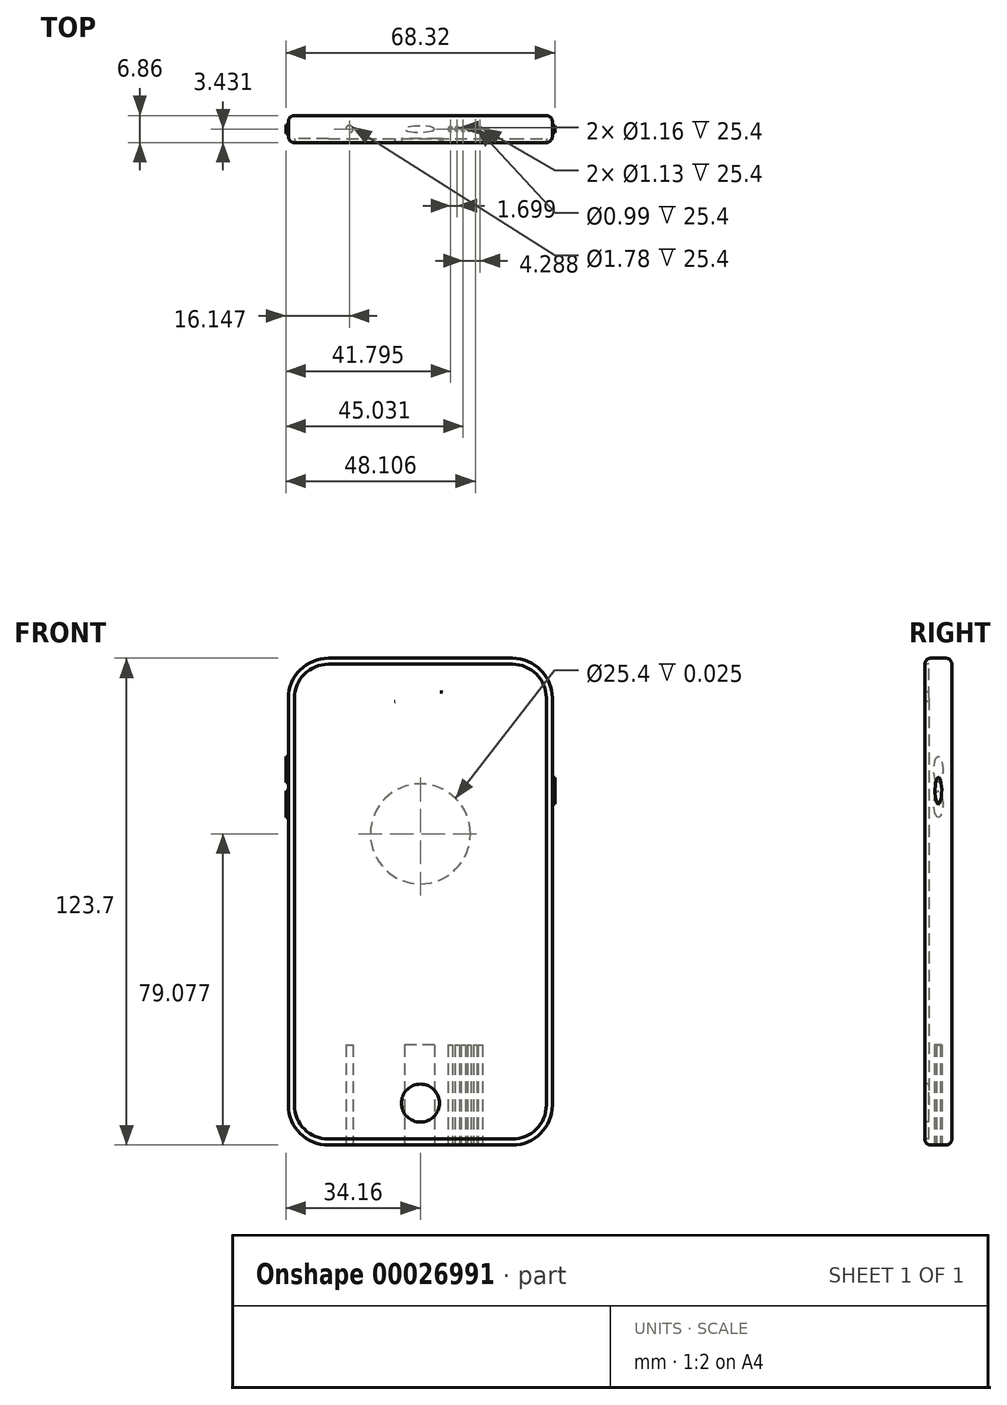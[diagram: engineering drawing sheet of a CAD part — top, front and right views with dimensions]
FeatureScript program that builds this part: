
annotation { "Feature Type Name" : "Feature", "Feature Type Description" : "" }
export const myFeature = defineFeature(function(context is Context, id is Id, definition is map)
    precondition{}
    {
        {
            var Q0;
            Q0=qCreatedBy(makeId("Front.planeOp"),FACE);
            var sketch = newSketch(context, id + "F0", { "sketchPlane" : qUnion([Q0])});
            skLineSegment(sketch, "E0.bottom", {"start": v(-33.33, 66.72) * mm, "end": v(33.73, 66.72) * mm});
            skLineSegment(sketch, "E0.top", {"start": v(-33.33, -56.98) * mm, "end": v(33.73, -56.98) * mm});
            skLineSegment(sketch, "E0.left", {"start": v(-33.33, 66.72) * mm, "end": v(-33.33, -56.98) * mm});
            skLineSegment(sketch, "E0.right", {"start": v(33.73, 66.72) * mm, "end": v(33.73, -56.98) * mm});
            skSolve(sketch);
        }
        {
            var Q0;
            Q0 = qSketchRegion(id + "F0", true);
            extrude(context, id + "F1", {"entities" : qUnion([Q0]), "depth" : 6.86 * mm});
        }
        {
            var Q0;
            Q0=makeQuery(id+"F1.opExtrude","SWEPT_EDGE",EDGE,{"disambiguationData":[OSD([sQuery(id+"F0.wireOp",EDGE,"E0.bottom"),sQuery(id+"F0.wireOp",EDGE,"E0.left")])]});
            var Q1;
            Q1=makeQuery(id+"F1.opExtrude","SWEPT_EDGE",EDGE,{"disambiguationData":[OSD([sQuery(id+"F0.wireOp",EDGE,"E0.bottom"),sQuery(id+"F0.wireOp",EDGE,"E0.right")])]});
            fillet(context, id + "F2", {"entities" : qUnion([Q0, Q1]), "radius" : 10.16 * mm, "tangentPropagation" : true, "allowEdgeOverflow" : false});
        }
        {
            var Q0;
            Q0=makeQuery(id+"F1.opExtrude","SWEPT_EDGE",EDGE,{"disambiguationData":[OSD([sQuery(id+"F0.wireOp",EDGE,"E0.top"),sQuery(id+"F0.wireOp",EDGE,"E0.left")])]});
            var Q1;
            Q1=makeQuery(id+"F1.opExtrude","SWEPT_EDGE",EDGE,{"disambiguationData":[OSD([sQuery(id+"F0.wireOp",EDGE,"E0.top"),sQuery(id+"F0.wireOp",EDGE,"E0.right")])]});
            fillet(context, id + "F3", {"entities" : qUnion([Q0, Q1]), "radius" : 10.16 * mm, "tangentPropagation" : true, "allowEdgeOverflow" : false});
        }
        {
            var Q0;
            Q0=makeQuery(id+"F1.opExtrude","CAP_EDGE",EDGE,{"disambiguationData":[OSD([sQuery(id+"F0.wireOp",EDGE,"E0.right")])],"isStart":true});
            fillet(context, id + "F4", {"entities" : qUnion([Q0]), "radius" : 1.52 * mm, "tangentPropagation" : true, "allowEdgeOverflow" : false});
        }
        {
            var Q0;
            Q0=makeQuery(id+"F1.opExtrude","CAP_EDGE",EDGE,{"disambiguationData":[OSD([sQuery(id+"F0.wireOp",EDGE,"E0.right")])],"isStart":false});
            fillet(context, id + "F5", {"entities" : qUnion([Q0]), "radius" : 1.52 * mm, "tangentPropagation" : true, "allowEdgeOverflow" : false});
        }
        {
            var Q0;
            Q0=makeQuery(id+"F1.opExtrude","CAP_FACE",FACE,{"disambiguationData":[OSD([sQuery(id+"F0.wireOp",EDGE,"E0.bottom"),sQuery(id+"F0.wireOp",EDGE,"E0.top"),sQuery(id+"F0.wireOp",EDGE,"E0.left"),sQuery(id+"F0.wireOp",EDGE,"E0.right")])],"isStart":false});
            var sketch = newSketch(context, id + "F6", { "sketchPlane" : qUnion([Q0])});
            skLineSegment(sketch, "E1.0", {"start": v(30.68, 48.43) * mm, "end": v(-30.28, 48.43) * mm});
            skLineSegment(sketch, "E2.0", {"start": v(-30.28, -38.7) * mm, "end": v(30.68, -38.7) * mm});
            skLineSegment(sketch, "E3.0", {"start": v(-30.28, 48.43) * mm, "end": v(-30.28, -38.7) * mm});
            skLineSegment(sketch, "E4.0", {"start": v(30.68, -38.7) * mm, "end": v(30.68, 48.43) * mm});
            skCircle(sketch, "E5", {"center": v(0.2, -46.31) * mm, "radius": 5.46 * mm});
            skLineSegment(sketch, "E6.0", {"start": v(23.57, 56.81) * mm, "end": v(6.78, 56.81) * mm});
            skCircle(sketch, "E7", {"center": v(-15.3, 56.81) * mm, "radius": 2.54 * mm});
            skCircle(sketch, "E8", {"center": v(0, 61.1) * mm, "radius": 1.12 * mm});
            skLineSegment(sketch, "E9", {"start": v(-6.37, 55.68) * mm, "end": v(5.57, 55.68) * mm});
            skLineSegment(sketch, "E10", {"start": v(5.86, 58.11) * mm, "end": v(-6.43, 58.11) * mm});
            skArc(sketch, "E11", {"start": v(-6.14, 58.11) * mm, "mid": v(-7.5, 56.93) * mm, "end": v(-6.2, 55.68) * mm});
            skArc(sketch, "E12", {"start": v(5.53, 55.68) * mm, "mid": v(6.77, 57.07) * mm, "end": v(5.23, 58.11) * mm});
            skPoint(sketch, "E13.orphan", {"position": v(-10.28, 58.11) * mm});
            skPoint(sketch, "E14.end.orphan", {"position": v(9.44, 58.11) * mm});
            skLineSegment(sketch, "E15.trimOffspring", {"start": v(-7.5, 56.81) * mm, "end": v(-23.17, 56.81) * mm});
            skCircle(sketch, "E16", {"center": v(0.2, -46.31) * mm, "radius": 4.82 * mm});
            skSolve(sketch);
        }
        {
            var Q0;
            Q0=makeQuery(id+"F6.imprint","IMPRINT",FACE,{"disambiguationData":[TD([[makeQuery(id+"F6.imprint","IMPRINT",EDGE,{"derivedFrom":sQuery(id+"F6.wireOp",EDGE,"E8")}),1.0]])]});
            var Q1;
            Q1=makeQuery(id+"F6.imprint","IMPRINT",FACE,{"disambiguationData":[TD([[makeQuery(id+"F6.imprint","IMPRINT",EDGE,{"derivedFrom":sQuery(id+"F6.wireOp",EDGE,"E5")}),1.0]])]});
            var Q2;
            {var subQ0=sQuery(id+"F6.wireOp",EDGE,"E15.trimOffspring");var subQ1=sQuery(id+"F6.wireOp",EDGE,"E7");var subQ3=makeQuery(id+"F6.imprint","INTERSECT",VERTEX,{"disambiguationData":[OD(0.0)],"derivedFrom":[subQ1,subQ0]});Q2=makeQuery(id+"F6.imprint","IMPRINT",FACE,{"disambiguationData":[TD([[makeQuery(id+"F6.imprint","IMPRINT",EDGE,{"disambiguationData":[TD([[subQ3,1.0]])],"derivedFrom":subQ1}),1.0]])]});}
            var Q3;
            {var subQ0=sQuery(id+"F6.wireOp",EDGE,"E15.trimOffspring");var subQ1=sQuery(id+"F6.wireOp",EDGE,"E7");var subQ3=makeQuery(id+"F6.imprint","INTERSECT",VERTEX,{"disambiguationData":[OD(0.0)],"derivedFrom":[subQ1,subQ0]});Q3=makeQuery(id+"F6.imprint","IMPRINT",FACE,{"disambiguationData":[TD([[makeQuery(id+"F6.imprint","IMPRINT",EDGE,{"disambiguationData":[TD([[subQ3,-1.0]])],"derivedFrom":subQ1}),1.0]])]});}
            var Q4;
            {var subQ0=sQuery(id+"F6.wireOp",EDGE,"E11");var subQ1=sQuery(id+"F6.wireOp",EDGE,"E9");var subQ3=makeQuery(id+"F6.imprint","INTERSECT",VERTEX,{"disambiguationData":[OD(0.0)],"derivedFrom":[subQ1,subQ0]});Q4=makeQuery(id+"F6.imprint","IMPRINT",FACE,{"disambiguationData":[TD([[makeQuery(id+"F6.imprint","IMPRINT",EDGE,{"disambiguationData":[TD([[subQ3,-1.0]])],"derivedFrom":subQ1}),-1.0]])]});}
            var Q5;
            {var subQ0=sQuery(id+"F6.wireOp",EDGE,"E12");var subQ1=sQuery(id+"F6.wireOp",EDGE,"E9");var subQ3=makeQuery(id+"F6.imprint","INTERSECT",VERTEX,{"disambiguationData":[OD(0.0)],"derivedFrom":[subQ1,subQ0]});Q5=makeQuery(id+"F6.imprint","IMPRINT",FACE,{"disambiguationData":[TD([[makeQuery(id+"F6.imprint","IMPRINT",EDGE,{"disambiguationData":[TD([[subQ3,1.0]])],"derivedFrom":subQ1}),-1.0]])]});}
            var Q6;
            {var subQ0=sQuery(id+"F6.wireOp",EDGE,"E12");var subQ1=sQuery(id+"F6.wireOp",EDGE,"E10");var subQ3=makeQuery(id+"F6.imprint","INTERSECT",VERTEX,{"disambiguationData":[OD(0.0)],"derivedFrom":[subQ1,subQ0]});Q6=makeQuery(id+"F6.imprint","IMPRINT",FACE,{"disambiguationData":[TD([[makeQuery(id+"F6.imprint","IMPRINT",EDGE,{"disambiguationData":[TD([[subQ3,-1.0]])],"derivedFrom":subQ1}),-1.0]])]});}
            var Q7;
            {var subQ0=sQuery(id+"F6.wireOp",EDGE,"E11");var subQ1=sQuery(id+"F6.wireOp",EDGE,"E10");var subQ3=makeQuery(id+"F6.imprint","INTERSECT",VERTEX,{"disambiguationData":[OD(0.0)],"derivedFrom":[subQ1,subQ0]});Q7=makeQuery(id+"F6.imprint","IMPRINT",FACE,{"disambiguationData":[TD([[makeQuery(id+"F6.imprint","IMPRINT",EDGE,{"disambiguationData":[TD([[subQ3,1.0]])],"derivedFrom":subQ1}),-1.0]])]});}
            var Q8;
            {var subQ0=sQuery(id+"F6.wireOp",EDGE,"E11");var subQ1=makeQuery(id+"F6.imprint","IMPRINT",VERTEX,{"derivedFrom":subQ0});Q8=makeQuery(id+"F6.imprint","IMPRINT",FACE,{"disambiguationData":[TD([[makeQuery(id+"F6.imprint","IMPRINT",EDGE,{"disambiguationData":[TD([[subQ1,1.0]])],"derivedFrom":subQ0}),1.0]])]});}
            var Q9;
            Q9=makeQuery(id+"F6.imprint","IMPRINT",FACE,{"disambiguationData":[TD([[makeQuery(id+"F6.imprint","IMPRINT",EDGE,{"derivedFrom":sQuery(id+"F6.wireOp",EDGE,"E1.0")}),1.0]])]});
            extrude(context, id + "F7", {"entities" : qUnion([Q0, Q1, Q2, Q3, Q4, Q5, Q6, Q7, Q8, Q9]), "operationType" : NewBodyOperationType.REMOVE, "oppositeDirection" : true, "depth" : 1.02 * mm});
        }
        {
            var Q0;
            Q0=makeQuery(id+"F1.opExtrude","SWEPT_FACE",FACE,{"disambiguationData":[OSD([sQuery(id+"F0.wireOp",EDGE,"E0.top")])]});
            var sketch = newSketch(context, id + "F8", { "sketchPlane" : qUnion([Q0])});
            skLineSegment(sketch, "E17", {"start": v(-23.17, 5.33) * mm, "end": v(-23.17, 1.52) * mm});
            skCircle(sketch, "E18", {"center": v(-17.81, 3.43) * mm, "radius": 0.9 * mm});
            skLineSegment(sketch, "E19", {"start": v(-23.17, 5.33) * mm, "end": v(23.57, 5.33) * mm});
            skEllipse(sketch, "E20", {"center": v(0, 3.43) * mm, "majorRadius": 3.79 * mm, "minorRadius": 0.94 * mm, "majorAxis": v(1, 0)});
            skCircle(sketch, "E21", {"center": v(7.83, 3.43) * mm, "radius": 0.58 * mm});
            skCircle(sketch, "E22", {"center": v(9.53, 3.43) * mm, "radius": 0.58 * mm});
            skCircle(sketch, "E23", {"center": v(11.07, 3.43) * mm, "radius": 0.56 * mm});
            skCircle(sketch, "E24", {"center": v(12.6, 3.43) * mm, "radius": 0.49 * mm});
            skCircle(sketch, "E25", {"center": v(14.15, 3.43) * mm, "radius": 0.5 * mm});
            skCircle(sketch, "E26", {"center": v(15.36, 3.43) * mm, "radius": 0.56 * mm});
            skSolve(sketch);
        }
        {
            var Q0;
            Q0=makeQuery(id+"F8.imprint","IMPRINT",FACE,{"disambiguationData":[TD([[makeQuery(id+"F8.imprint","IMPRINT",EDGE,{"derivedFrom":sQuery(id+"F8.wireOp",EDGE,"E18")}),1.0]])]});
            var Q1;
            Q1=makeQuery(id+"F8.imprint","IMPRINT",FACE,{"disambiguationData":[TD([[makeQuery(id+"F8.imprint","IMPRINT",EDGE,{"derivedFrom":sQuery(id+"F8.wireOp",EDGE,"E20")}),1.0]])]});
            var Q2;
            Q2=makeQuery(id+"F8.imprint","IMPRINT",FACE,{"disambiguationData":[TD([[makeQuery(id+"F8.imprint","IMPRINT",EDGE,{"derivedFrom":sQuery(id+"F8.wireOp",EDGE,"E22")}),1.0]])]});
            var Q3;
            Q3=makeQuery(id+"F8.imprint","IMPRINT",FACE,{"disambiguationData":[TD([[makeQuery(id+"F8.imprint","IMPRINT",EDGE,{"derivedFrom":sQuery(id+"F8.wireOp",EDGE,"E23")}),1.0]])]});
            var Q4;
            Q4=makeQuery(id+"F8.imprint","IMPRINT",FACE,{"disambiguationData":[TD([[makeQuery(id+"F8.imprint","IMPRINT",EDGE,{"derivedFrom":sQuery(id+"F8.wireOp",EDGE,"E24")}),1.0]])]});
            var Q5;
            Q5=makeQuery(id+"F8.imprint","IMPRINT",FACE,{"disambiguationData":[TD([[makeQuery(id+"F8.imprint","IMPRINT",EDGE,{"derivedFrom":sQuery(id+"F8.wireOp",EDGE,"E25")}),1.0]])]});
            var Q6;
            Q6=makeQuery(id+"F8.imprint","IMPRINT",FACE,{"disambiguationData":[TD([[makeQuery(id+"F8.imprint","IMPRINT",EDGE,{"derivedFrom":sQuery(id+"F8.wireOp",EDGE,"E26")}),1.0]])]});
            var Q7;
            Q7=makeQuery(id+"F8.imprint","IMPRINT",FACE,{"disambiguationData":[TD([[makeQuery(id+"F8.imprint","IMPRINT",EDGE,{"derivedFrom":sQuery(id+"F8.wireOp",EDGE,"E21")}),1.0]])]});
            extrude(context, id + "F9", {"entities" : qUnion([Q0, Q1, Q2, Q3, Q4, Q5, Q6, Q7]), "operationType" : NewBodyOperationType.REMOVE, "oppositeDirection" : true, "depth" : 25.4 * mm});
        }
        {
            var Q0;
            Q0=makeQuery(id+"F1.opExtrude","SWEPT_FACE",FACE,{"disambiguationData":[OSD([sQuery(id+"F0.wireOp",EDGE,"E0.right")])]});
            var sketch = newSketch(context, id + "F10", { "sketchPlane" : qUnion([Q0])});
            skEllipse(sketch, "E27", {"center": v(-3.43, 33.07) * mm, "majorRadius": 3.36 * mm, "minorRadius": 0.85 * mm, "majorAxis": v(0, -1)});
            skSolve(sketch);
        }
        {
            var Q0;
            Q0=makeQuery(id+"F10.imprint","IMPRINT",FACE,{"disambiguationData":[TD([[makeQuery(id+"F10.imprint","IMPRINT",EDGE,{"derivedFrom":sQuery(id+"F10.wireOp",EDGE,"E27")}),1.0]])]});
            extrude(context, id + "F11", {"entities" : qUnion([Q0]), "operationType" : NewBodyOperationType.ADD, "depth" : 0.64 * mm});
        }
        {
            var Q0;
            Q0=makeQuery(id+"F1.opExtrude","SWEPT_FACE",FACE,{"disambiguationData":[OSD([sQuery(id+"F0.wireOp",EDGE,"E0.left")])]});
            var sketch = newSketch(context, id + "F12", { "sketchPlane" : qUnion([Q0])});
            skEllipse(sketch, "E28", {"center": v(3.43, 38.42) * mm, "majorRadius": 3.32 * mm, "minorRadius": 1.12 * mm, "majorAxis": v(0, -1)});
            skEllipse(sketch, "E29", {"center": v(3.43, 29.66) * mm, "majorRadius": 3.35 * mm, "minorRadius": 1.12 * mm, "majorAxis": v(0, -1)});
            skSolve(sketch);
        }
        {
            var Q0;
            Q0 = qSketchRegion(id + "F12", true);
            extrude(context, id + "F13", {"entities" : qUnion([Q0]), "operationType" : NewBodyOperationType.ADD, "depth" : 0.64 * mm});
        }
        {
            var Q0;
            Q0=makeQuery(id+"F1.opExtrude","CAP_FACE",FACE,{"disambiguationData":[OSD([sQuery(id+"F0.wireOp",EDGE,"E0.bottom"),sQuery(id+"F0.wireOp",EDGE,"E0.top"),sQuery(id+"F0.wireOp",EDGE,"E0.left"),sQuery(id+"F0.wireOp",EDGE,"E0.right")])],"isStart":true});
            var sketch = newSketch(context, id + "F14", { "sketchPlane" : qUnion([Q0])});
            skCircle(sketch, "E30", {"center": v(-0.2, 22.1) * mm, "radius": 12.7 * mm});
            skSolve(sketch);
        }
        {
            var Q0;
            Q0=makeQuery(id+"F14.imprint","IMPRINT",FACE,{"disambiguationData":[TD([[makeQuery(id+"F14.imprint","IMPRINT",EDGE,{"derivedFrom":sQuery(id+"F14.wireOp",EDGE,"E30")}),1.0]])]});
            extrude(context, id + "F15", {"entities" : qUnion([Q0]), "operationType" : NewBodyOperationType.REMOVE, "oppositeDirection" : true, "depth" : 0.03 * mm});
        }
    });
